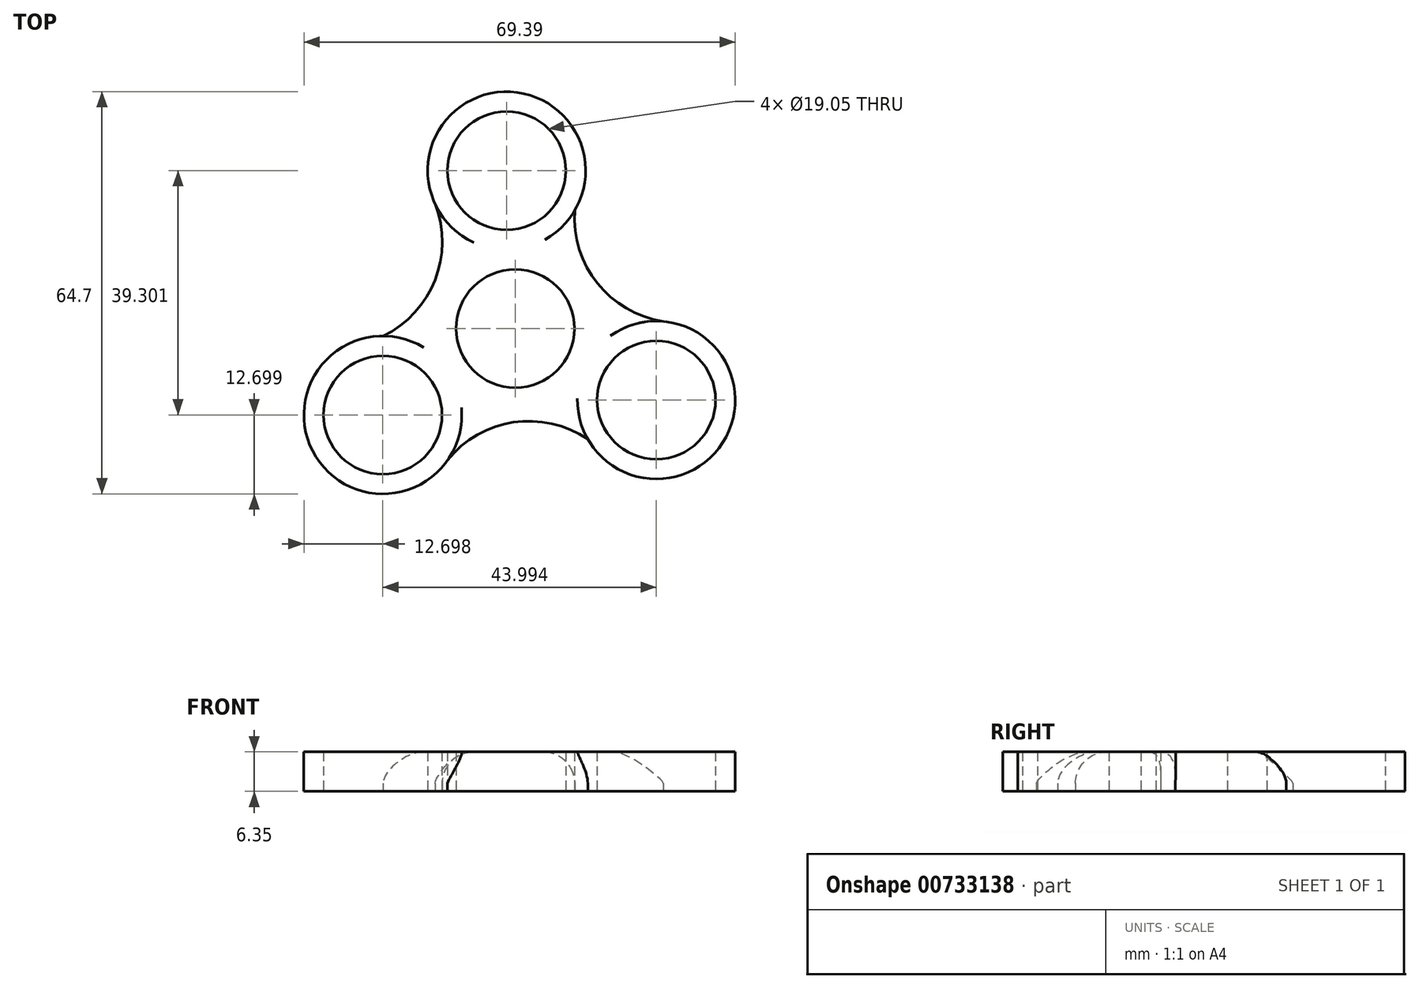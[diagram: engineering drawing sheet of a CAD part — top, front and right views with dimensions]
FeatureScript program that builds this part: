
annotation { "Feature Type Name" : "Feature", "Feature Type Description" : "" }
export const myFeature = defineFeature(function(context is Context, id is Id, definition is map)
    precondition{}
    {
        {
            var Q0;
            Q0=qCreatedBy(makeId("Top.planeOp"),FACE);
            var sketch = newSketch(context, id + "F0", { "sketchPlane" : qUnion([Q0])});
            skCircle(sketch, "E0", {"center": v(-4, 14.84) * mm, "radius": 9.53 * mm});
            skCircle(sketch, "E1", {"center": v(-5.4, 40.24) * mm, "radius": 9.53 * mm});
            skCircle(sketch, "E2.1.0", {"center": v(-25.31, 0.94) * mm, "radius": 9.53 * mm});
            skCircle(sketch, "E2.2.0", {"center": v(18.68, 3.34) * mm, "radius": 9.53 * mm});
            skArc(sketch, "E3.0", {"start": v(-25.25, 13.64) * mm, "mid": v(-36.6, -4.89) * mm, "end": v(-14.92, -6.36) * mm});
            skArc(sketch, "E4.0", {"start": v(5.57, 33.83) * mm, "mid": v(-4.8, 52.93) * mm, "end": v(-16.92, 34.9) * mm});
            skArc(sketch, "E5.0", {"start": v(7.65, -2.95) * mm, "mid": v(29.37, -3.52) * mm, "end": v(19.81, 16) * mm});
            skArc(sketch, "E6", {"start": v(-25.25, 13.64) * mm, "mid": v(-16.77, 23.06) * mm, "end": v(-17.27, 35.73) * mm});
            skArc(sketch, "E7.1.0", {"start": v(7.65, -2.95) * mm, "mid": v(-4.75, -0.32) * mm, "end": v(-15.47, -7.09) * mm});
            skArc(sketch, "E7.2.0", {"start": v(5.57, 33.83) * mm, "mid": v(9.5, 21.78) * mm, "end": v(20.71, 15.88) * mm});
            skSolve(sketch);
        }
        {
            var Q0;
            Q0 = qSketchRegion(id + "F0", true);
            extrude(context, id + "F1", {"entities" : qUnion([Q0]), "depth" : 6.35 * mm, "offsetDistance" : 25.4 * mm});
        }
        {
            var Q0;
            Q0=makeQuery(id+"F1.opExtrude","CAP_EDGE",EDGE,{"disambiguationData":[OSD([sQuery(id+"F0.wireOp",EDGE,"E7.1.0")])],"isStart":false});
            var Q1;
            Q1=makeQuery(id+"F1.opExtrude","CAP_EDGE",EDGE,{"disambiguationData":[OSD([sQuery(id+"F0.wireOp",EDGE,"E7.2.0")])],"isStart":false});
            var Q2;
            Q2=makeQuery(id+"F1.opExtrude","CAP_EDGE",EDGE,{"disambiguationData":[OSD([sQuery(id+"F0.wireOp",EDGE,"E6")])],"isStart":false});
            fillet(context, id + "F2", {"entities" : qUnion([Q0, Q1, Q2]), "radius" : 5.08 * mm, "tangentPropagation" : true, "allowEdgeOverflow" : false});
        }
    });
